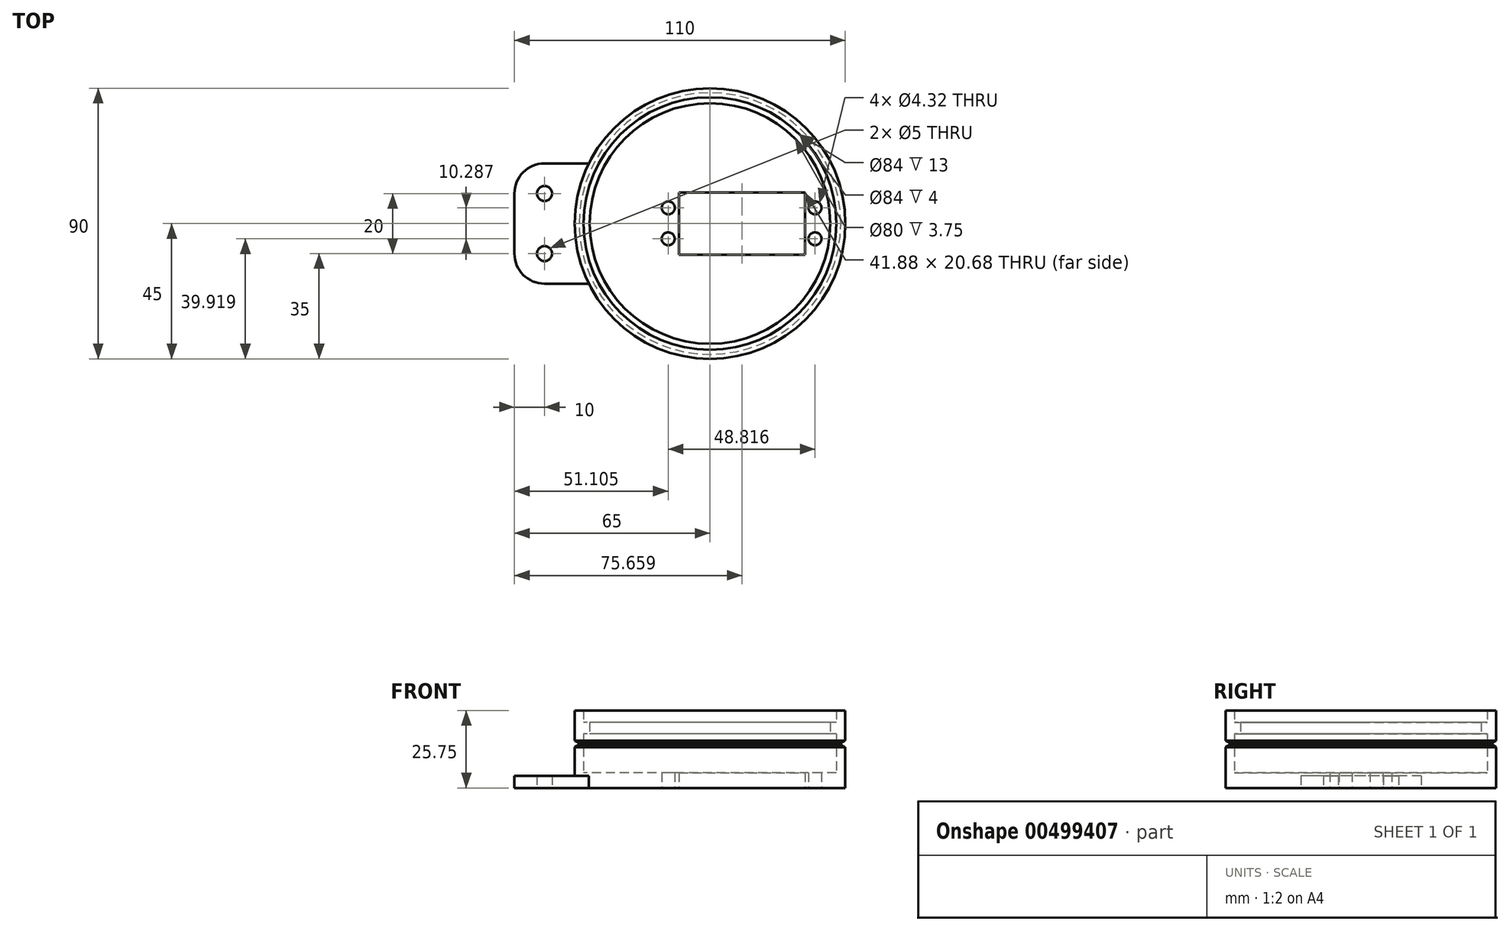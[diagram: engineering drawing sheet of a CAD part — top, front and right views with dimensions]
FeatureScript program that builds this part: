
annotation { "Feature Type Name" : "Feature", "Feature Type Description" : "" }
export const myFeature = defineFeature(function(context is Context, id is Id, definition is map)
    precondition{}
    {
        {
            var Q0;
            Q0=qCreatedBy(makeId("Top.planeOp"),FACE);
            var sketch = newSketch(context, id + "F0", { "sketchPlane" : qUnion([Q0])});
            skLineSegment(sketch, "E0.0", {"start": v(-10.28, 10.34) * mm, "end": v(31.6, 10.34) * mm});
            skCircle(sketch, "E0.1", {"center": v(34.92, 5.2) * mm, "radius": 2.16 * mm});
            skCircle(sketch, "E0.2", {"center": v(34.92, -5.08) * mm, "radius": 2.16 * mm});
            skLineSegment(sketch, "E0.3", {"start": v(31.6, 10.34) * mm, "end": v(31.6, -10.34) * mm});
            skLineSegment(sketch, "E0.4", {"start": v(-10.28, -10.34) * mm, "end": v(-10.28, 10.34) * mm});
            skCircle(sketch, "E0.5", {"center": v(-13.84, 5.2) * mm, "radius": 2.16 * mm});
            skCircle(sketch, "E0.6", {"center": v(-13.9, -5.08) * mm, "radius": 2.16 * mm});
            skLineSegment(sketch, "E0.7", {"start": v(-10.28, -10.34) * mm, "end": v(31.6, -10.34) * mm});
            skPoint(sketch, "E1.centerSnap0", {"position": v(-10.28, 0) * mm});
            skPoint(sketch, "E1.centerSnap1", {"position": v(10.66, 10.34) * mm});
            skCircle(sketch, "E2", {"center": v(0, 0) * mm, "radius": 1 * mm});
            skPoint(sketch, "E3.startSnap0", {"position": v(31.6, 0) * mm});
            skCircle(sketch, "E4", {"center": v(0, 0) * mm, "radius": 45 * mm});
            skLineSegment(sketch, "E5", {"start": v(-20.62, 40) * mm, "end": v(20.62, 40) * mm});
            skLineSegment(sketch, "E6.1.0", {"start": v(-24.33, -37.85) * mm, "end": v(-44.95, -2.15) * mm});
            skLineSegment(sketch, "E6.2.0", {"start": v(44.95, -2.15) * mm, "end": v(24.33, -37.85) * mm});
            skCircle(sketch, "E7", {"center": v(0, 0) * mm, "radius": 40 * mm});
            skLineSegment(sketch, "E8", {"start": v(-20.62, 40) * mm, "end": v(-26.35, 37.05) * mm});
            skLineSegment(sketch, "E9", {"start": v(-20.62, 40) * mm, "end": v(-18.32, 35.56) * mm});
            skLineSegment(sketch, "E10", {"start": v(20.62, 40) * mm, "end": v(18.32, 35.56) * mm});
            skLineSegment(sketch, "E11.1.0", {"start": v(-44.95, -2.15) * mm, "end": v(-39.95, -1.9) * mm});
            skLineSegment(sketch, "E11.1.1", {"start": v(-24.33, -37.85) * mm, "end": v(-21.63, -33.65) * mm});
            skLineSegment(sketch, "E11.2.0", {"start": v(24.33, -37.85) * mm, "end": v(21.63, -33.65) * mm});
            skLineSegment(sketch, "E11.2.1", {"start": v(44.95, -2.15) * mm, "end": v(39.95, -1.9) * mm});
            skSolve(sketch);
        }
        {
            var Q0;
            Q0=makeQuery(id+"F0.imprint","IMPRINT",FACE,{"disambiguationData":[TD([[makeQuery(id+"F0.imprint","IMPRINT",EDGE,{"derivedFrom":sQuery(id+"F0.wireOp",EDGE,"E0.0")}),1.0]])]});
            var Q1;
            {var subQ0=sQuery(id+"F0.wireOp",EDGE,"E9");Q1=makeQuery(id+"F0.imprint","IMPRINT",FACE,{"disambiguationData":[TD([[makeQuery(id+"F0.imprint","IMPRINT",EDGE,{"derivedFrom":subQ0}),1.0]])]});}
            var Q2;
            {var subQ0=sQuery(id+"F0.wireOp",EDGE,"E10");Q2=makeQuery(id+"F0.imprint","IMPRINT",FACE,{"disambiguationData":[TD([[makeQuery(id+"F0.imprint","IMPRINT",EDGE,{"derivedFrom":subQ0}),-1.0]])]});}
            var Q3;
            {var subQ0=sQuery(id+"F0.wireOp",EDGE,"E5");var subQ4=makeQuery(id+"F0.imprint","INTERSECT",VERTEX,{"derivedFrom":[subQ0,sQuery(id+"F0.wireOp",EDGE,"E7")]});Q3=makeQuery(id+"F0.imprint","IMPRINT",FACE,{"disambiguationData":[TD([[makeQuery(id+"F0.imprint","IMPRINT",EDGE,{"disambiguationData":[TD([[subQ4,1.0]])],"derivedFrom":subQ0}),1.0]])]});}
            var Q4;
            {var subQ0=sQuery(id+"F0.wireOp",EDGE,"E9");Q4=makeQuery(id+"F0.imprint","IMPRINT",FACE,{"disambiguationData":[TD([[makeQuery(id+"F0.imprint","IMPRINT",EDGE,{"derivedFrom":subQ0}),-1.0]])]});}
            var Q5;
            {var subQ0=sQuery(id+"F0.wireOp",EDGE,"E10");Q5=makeQuery(id+"F0.imprint","IMPRINT",FACE,{"disambiguationData":[TD([[makeQuery(id+"F0.imprint","IMPRINT",EDGE,{"derivedFrom":subQ0}),1.0]])]});}
            var Q6;
            {var subQ0=sQuery(id+"F0.wireOp",EDGE,"E11.2.1");Q6=makeQuery(id+"F0.imprint","IMPRINT",FACE,{"disambiguationData":[TD([[makeQuery(id+"F0.imprint","IMPRINT",EDGE,{"derivedFrom":subQ0}),1.0]])]});}
            var Q7;
            {var subQ0=sQuery(id+"F0.wireOp",EDGE,"E6.2.0");var subQ4=makeQuery(id+"F0.imprint","INTERSECT",VERTEX,{"derivedFrom":[subQ0,sQuery(id+"F0.wireOp",EDGE,"E7")]});Q7=makeQuery(id+"F0.imprint","IMPRINT",FACE,{"disambiguationData":[TD([[makeQuery(id+"F0.imprint","IMPRINT",EDGE,{"disambiguationData":[TD([[subQ4,1.0]])],"derivedFrom":subQ0}),1.0]])]});}
            var Q8;
            {var subQ0=sQuery(id+"F0.wireOp",EDGE,"E11.2.0");Q8=makeQuery(id+"F0.imprint","IMPRINT",FACE,{"disambiguationData":[TD([[makeQuery(id+"F0.imprint","IMPRINT",EDGE,{"derivedFrom":subQ0}),-1.0]])]});}
            var Q9;
            {var subQ0=sQuery(id+"F0.wireOp",EDGE,"E11.1.1");Q9=makeQuery(id+"F0.imprint","IMPRINT",FACE,{"disambiguationData":[TD([[makeQuery(id+"F0.imprint","IMPRINT",EDGE,{"derivedFrom":subQ0}),-1.0]])]});}
            var Q10;
            {var subQ0=sQuery(id+"F0.wireOp",EDGE,"E11.1.1");Q10=makeQuery(id+"F0.imprint","IMPRINT",FACE,{"disambiguationData":[TD([[makeQuery(id+"F0.imprint","IMPRINT",EDGE,{"derivedFrom":subQ0}),1.0]])]});}
            var Q11;
            {var subQ0=sQuery(id+"F0.wireOp",EDGE,"E11.1.0");Q11=makeQuery(id+"F0.imprint","IMPRINT",FACE,{"disambiguationData":[TD([[makeQuery(id+"F0.imprint","IMPRINT",EDGE,{"derivedFrom":subQ0}),-1.0]])]});}
            var Q12;
            {var subQ0=sQuery(id+"F0.wireOp",EDGE,"E6.1.0");var subQ4=makeQuery(id+"F0.imprint","INTERSECT",VERTEX,{"derivedFrom":[subQ0,sQuery(id+"F0.wireOp",EDGE,"E7")]});Q12=makeQuery(id+"F0.imprint","IMPRINT",FACE,{"disambiguationData":[TD([[makeQuery(id+"F0.imprint","IMPRINT",EDGE,{"disambiguationData":[TD([[subQ4,1.0]])],"derivedFrom":subQ0}),1.0]])]});}
            extrude(context, id + "F1", {"entities" : qUnion([Q0, Q1, Q2, Q3, Q4, Q5, Q6, Q7, Q8, Q9, Q10, Q11, Q12]), "depth" : 5 * mm, "offsetDistance" : 25 * mm});
        }
        {
            var Q0;
            Q0=makeQuery(id+"F1.opExtrude","CAP_FACE",FACE,{"disambiguationData":[OSD([sQuery(id+"F0.wireOp",EDGE,"E0.0"),sQuery(id+"F0.wireOp",EDGE,"E0.1"),sQuery(id+"F0.wireOp",EDGE,"E0.2"),sQuery(id+"F0.wireOp",EDGE,"E0.3"),sQuery(id+"F0.wireOp",EDGE,"E0.4"),sQuery(id+"F0.wireOp",EDGE,"E0.5"),sQuery(id+"F0.wireOp",EDGE,"E0.6"),sQuery(id+"F0.wireOp",EDGE,"E0.7"),sQuery(id+"F0.wireOp",EDGE,"E4")])],"isStart":false});
            var sketch = newSketch(context, id + "F2", { "sketchPlane" : qUnion([Q0])});
            skCircle(sketch, "E12", {"center": v(0, 0) * mm, "radius": 42 * mm});
            skCircle(sketch, "E13", {"center": v(0, 0) * mm, "radius": 40 * mm});
            skSolve(sketch);
        }
        {
            var Q0;
            Q0=makeQuery(id+"F2.imprint","IMPRINT",FACE,{"disambiguationData":[TD([[makeQuery(id+"F2.imprint","IMPRINT",EDGE,{"derivedFrom":sQuery(id+"F2.wireOp",EDGE,"E12")}),-1.0]])]});
            extrude(context, id + "F3", {"entities" : qUnion([Q0]), "operationType" : NewBodyOperationType.ADD, "depth" : 20.75 * mm, "offsetDistance" : 25 * mm});
        }
        {
            var Q0;
            Q0=makeQuery(id+"F2.imprint","IMPRINT",FACE,{"disambiguationData":[TD([[makeQuery(id+"F2.imprint","IMPRINT",EDGE,{"derivedFrom":sQuery(id+"F2.wireOp",EDGE,"E12")}),1.0]])]});
            extrude(context, id + "F4", {"entities" : qUnion([Q0]), "operationType" : NewBodyOperationType.ADD, "depth" : 16.75 * mm, "offsetDistance" : 25 * mm, "hasSecondDirection" : true, "secondDirectionOppositeDirection" : false, "secondDirectionDepth" : 13 * mm});
        }
        {
            var Q0;
            Q0=qCreatedBy(makeId("Top.planeOp"),FACE);
            var sketch = newSketch(context, id + "F5", { "sketchPlane" : qUnion([Q0])});
            skCircle(sketch, "E14.0", {"center": v(0, 0) * mm, "radius": 45 * mm});
            skLineSegment(sketch, "E15.bottom", {"start": v(-65, 20) * mm, "end": v(-25, 20) * mm});
            skLineSegment(sketch, "E15.top", {"start": v(-65, -20) * mm, "end": v(-25, -20) * mm});
            skLineSegment(sketch, "E15.left", {"start": v(-65, 20) * mm, "end": v(-65, -20) * mm});
            skLineSegment(sketch, "E15.right", {"start": v(-25, 20) * mm, "end": v(-25, -20) * mm});
            skPoint(sketch, "E15.middle", {"position": v(-45, 0) * mm});
            skPoint(sketch, "E16", {"position": v(-65, 10) * mm});
            skPoint(sketch, "E17", {"position": v(-55, 20) * mm});
            skPoint(sketch, "E18", {"position": v(-65, -10) * mm});
            skCircle(sketch, "E19", {"center": v(-55, 10) * mm, "radius": 2.5 * mm});
            skCircle(sketch, "E20", {"center": v(-55, -10) * mm, "radius": 2.5 * mm});
            skSolve(sketch);
        }
        {
            var Q0;
            {var subQ0=sQuery(id+"F5.wireOp",EDGE,"E15.left");Q0=makeQuery(id+"F5.imprint","IMPRINT",FACE,{"disambiguationData":[TD([[makeQuery(id+"F5.imprint","IMPRINT",EDGE,{"derivedFrom":subQ0}),1.0]])]});}
            extrude(context, id + "F6", {"entities" : qUnion([Q0]), "operationType" : NewBodyOperationType.ADD, "depth" : 4 * mm, "offsetDistance" : 25 * mm});
        }
        {
            var Q0;
            Q0=makeQuery(id+"F6.opExtrude","SWEPT_EDGE",EDGE,{"disambiguationData":[OSD([sQuery(id+"F5.wireOp",EDGE,"E15.top"),sQuery(id+"F5.wireOp",EDGE,"E15.left")])]});
            var Q1;
            Q1=makeQuery(id+"F6.opExtrude","SWEPT_EDGE",EDGE,{"disambiguationData":[OSD([sQuery(id+"F5.wireOp",EDGE,"E14.0"),sQuery(id+"F5.wireOp",EDGE,"E15.top")])]});
            var Q2;
            Q2=makeQuery(id+"F6.opExtrude","SWEPT_EDGE",EDGE,{"disambiguationData":[OSD([sQuery(id+"F5.wireOp",EDGE,"E14.0"),sQuery(id+"F5.wireOp",EDGE,"E15.bottom")])]});
            var Q3;
            Q3=makeQuery(id+"F6.opExtrude","SWEPT_EDGE",EDGE,{"disambiguationData":[OSD([sQuery(id+"F5.wireOp",EDGE,"E15.bottom"),sQuery(id+"F5.wireOp",EDGE,"E15.left")])]});
            fillet(context, id + "F7", {"entities" : qUnion([Q0, Q1, Q2, Q3]), "radius" : 10 * mm, "tangentPropagation" : true, "allowEdgeOverflow" : false});
        }
        {
            var Q0;
            Q0=qCreatedBy(makeId("Right.planeOp"),FACE);
            var sketch = newSketch(context, id + "F8", { "sketchPlane" : qUnion([Q0])});
            skLineSegment(sketch, "E21", {"start": v(0, 0) * mm, "end": v(0, 74.26) * mm});
            skSolve(sketch);
        }
        {
            var Q0;
            Q0=qCreatedBy(makeId("Front.planeOp"),FACE);
            var sketch = newSketch(context, id + "F9", { "sketchPlane" : qUnion([Q0])});
            skLineSegment(sketch, "E22.0", {"start": v(-45, 25.75) * mm, "end": v(45, 25.75) * mm});
            skLineSegment(sketch, "E23", {"start": v(45, 25.75) * mm, "end": v(45, 0) * mm});
            skPoint(sketch, "E24", {"position": v(45, 15.75) * mm});
            skLineSegment(sketch, "E25", {"start": v(45, 15.75) * mm, "end": v(43.5, 15.75) * mm, "construction": true});
            skLineSegment(sketch, "E26", {"start": v(45, 15.75) * mm, "end": v(43.5, 14.88) * mm});
            skLineSegment(sketch, "E27", {"start": v(43.5, 14.88) * mm, "end": v(43.5, 14.38) * mm});
            skLineSegment(sketch, "E28", {"start": v(43.5, 14.38) * mm, "end": v(45, 13.52) * mm});
            skLineSegment(sketch, "E29", {"start": v(43.5, 14.38) * mm, "end": v(45, 14.38) * mm, "construction": true});
            skLineSegment(sketch, "E30.0", {"start": v(43.38, 14.31) * mm, "end": v(44.94, 13.4) * mm});
            skLineSegment(sketch, "E30.1", {"start": v(43.38, 14.96) * mm, "end": v(43.38, 14.31) * mm});
            skLineSegment(sketch, "E30.2", {"start": v(44.94, 15.86) * mm, "end": v(43.38, 14.96) * mm});
            skLineSegment(sketch, "E31", {"start": v(44.94, 15.86) * mm, "end": v(45, 15.9) * mm});
            skLineSegment(sketch, "E32", {"start": v(44.94, 13.4) * mm, "end": v(45, 13.37) * mm});
            skSolve(sketch);
        }
        {
            var Q0;
            Q0=qCreatedBy(makeId("Front.planeOp"),FACE);
            var sketch = newSketch(context, id + "F10", { "sketchPlane" : qUnion([Q0])});
            skLineSegment(sketch, "E33", {"start": v(0, 0) * mm, "end": v(0, 24.73) * mm});
            skSolve(sketch);
        }
        {
            var Q0;
            {var subQ0=sQuery(id+"F9.wireOp",EDGE,"E26");Q0=makeQuery(id+"F9.imprint","IMPRINT",FACE,{"disambiguationData":[TD([[makeQuery(id+"F9.imprint","IMPRINT",EDGE,{"derivedFrom":subQ0}),1.0]])]});}
            var Q1;
            Q1=sQuery(id+"F10.wireOp",EDGE,"E33");
            revolve(context, id + "F11", {"operationType" : NewBodyOperationType.REMOVE, "entities" : qUnion([Q0]), "axis" : qUnion([Q1]), "revolveType" : RevolveType.FULL, "oppositeDirection" : true});
        }
    });
